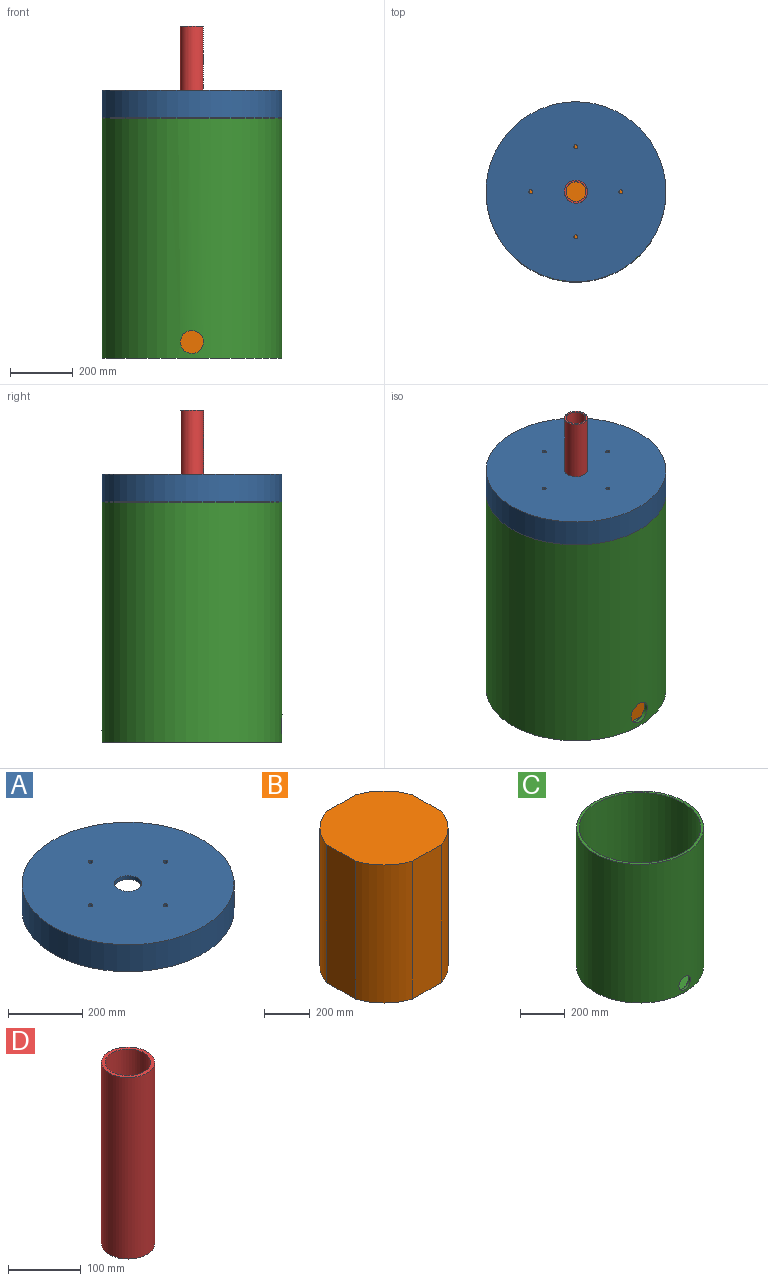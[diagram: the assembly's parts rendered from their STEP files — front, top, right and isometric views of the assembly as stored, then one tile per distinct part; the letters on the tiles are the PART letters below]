
ASSEMBLY  parts=4 mates=3
PART A: 10 faces, bbox 571.5x571.5x88.9 mm
  f0: cylinder r=6.35mm len=12.7mm, axis (0,0,-1), area 506.7mm2, adj f5,f8
  f1: cylinder r=6.35mm len=12.7mm, axis (0,0,-1), area 506.7mm2, adj f5,f8
  f2: cylinder r=6.35mm len=12.7mm, axis (0,0,-1), area 506.7mm2, adj f5,f8
  f3: cylinder r=6.35mm len=12.7mm, axis (0,0,-1), area 506.7mm2, adj f5,f8
  f4: cylinder r=285.75mm len=571.5mm, axis (0,0,-1), area 159612.9mm2, adj f5,f6
  f5: plane 571.5x571.5mm, normal (0,0,1), area 251825.7mm2, adj f0,f1,f2,f3,f4,f9
  f6: plane 571.5x571.5mm, normal (0,0,-1), area 22295.1mm2, adj f4,f7
  f7: cylinder r=273.05mm len=546.1mm, axis (0,0,-1), area 130730.5mm2, adj f6,f8
  f8: plane 546.1x546.1mm, normal (0,0,-1), area 229530.6mm2, adj f0,f1,f2,f3,f7,f9
  f9: cylinder r=36.51mm len=73.03mm, axis (0,0,1), area 2913.6mm2, adj f5,f8
PART B: 10 faces, bbox 529.6x529.6x736.6 mm
  f0: cylinder r=279.4mm len=736.6mm, axis (0,0,-1), area 189620.6mm2, adj f4,f5,f6,f9
  f1: cylinder r=279.4mm len=736.6mm, axis (0,0,-1), area 189620.6mm2, adj f4,f5,f8,f9
  f2: cylinder r=279.4mm len=736.6mm, axis (0,0,-1), area 189620.6mm2, adj f4,f5,f7,f8
  f3: cylinder r=279.4mm len=736.6mm, axis (0,0,-1), area 189620.6mm2, adj f4,f5,f6,f7
  f4: plane 529.6x529.6mm, normal (0,0,1), area 238267.5mm2, adj f0,f1,f2,f3,f6,f7,f8,f9
  f5: plane 529.6x529.6mm, normal (0,0,-1), area 238267.5mm2, adj f0,f1,f2,f3,f6,f7,f8,f9
  f6: plane 736.6x178.28mm, normal (1,0,0), area 131322.2mm2, adj f0,f3,f4,f5
  f7: plane 736.6x178.28mm, normal (0,-1,0), area 131322.2mm2, adj f2,f3,f4,f5
  f8: plane 736.6x178.28mm, normal (-1,0,0), area 131322.2mm2, adj f1,f2,f4,f5
  f9: plane 736.6x178.28mm, normal (0,1,0), area 131322.2mm2, adj f0,f1,f4,f5
PART C: 7 faces, bbox 571.5x571.5x762 mm
  f0: cylinder r=285.75mm len=762mm, axis (0,0,-1), area 1363337.3mm2, adj f2,f3,f5,f6
  f1: cylinder r=273.05mm len=749.3mm, axis (0,0,-1), area 1280743.1mm2, adj f2,f4,f5,f6
  f2: plane 571.5x571.5mm, normal (0,0,1), area 22295.1mm2, adj f0,f1
  f3: plane 571.5x571.5mm, normal (0,0,-1), area 256520.7mm2, adj f0
  f4: plane 546.1x546.1mm, normal (0,0,1), area 234225.5mm2, adj f1
  f5: cylinder r=36.51mm len=73.03mm, axis (0,1,0), area 2926.1mm2, adj f0,f1
  f6: cylinder r=13.33mm len=26.67mm, axis (0,-1,0), area 1064.7mm2, adj f0,f1
PART D: 4 faces, bbox 73x73x304.8 mm
  f0: cylinder r=31.36mm len=304.8mm, axis (0,0,-1), area 60050.9mm2, adj f2,f3
  f1: cylinder r=36.51mm len=304.8mm, axis (0,0,-1), area 69925.6mm2, adj f2,f3
  f2: plane 73.03x73.03mm, normal (0,0,1), area 1099.4mm2, adj f0,f1
  f3: plane 73.03x73.03mm, normal (0,0,-1), area 1099.4mm2, adj f0,f1
PLACE A t=(8.86,-396.22,704.4)mm
PLACE B rot(axis=(0.71,-0.71,0),180deg) t=(8.86,-396.22,691.7)mm
PLACE C t=(8.86,-396.22,-57.6)mm
PLACE D rot(axis=(0,0,-1),90deg) t=(8.86,-396.22,691.7)mm
MATE fastened D.f0 <-> B.f0  axis (0,0,-1) through (8.86,-396.22,691.7)mm
MATE fastened A.f4 <-> C.f0  axis (0,0,-1) through (8.86,-396.22,704.4)mm
MATE fastened B.f0 <-> C.f0  axis (0,0,-1) through (8.86,-396.22,-44.9)mm
